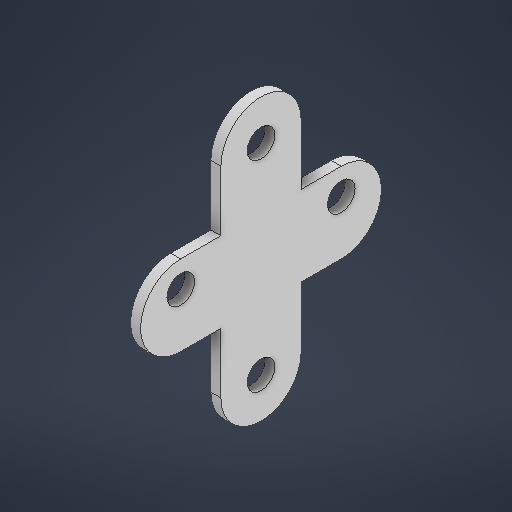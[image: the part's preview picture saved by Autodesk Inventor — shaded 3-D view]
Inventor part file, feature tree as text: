
AUTODESK INVENTOR PART (.ipt)
format: ipt  version: 2025.2 (Build 292293000, 293)  size: 212,992 bytes
history: native  units: in
note: dims shown in document units (in); Inventor stores cm internally (conversion verified against a paired STEP export)
features: extrude x1, sketch x1
ambient origin geometry x8: Origin, YZ Plane, XZ Plane, XY Plane, X Axis, Y Axis, Z Axis, Center Point
bodies: Solid1 (feature_tree)
feature tree (2):
  extrude  "Extrusion1"  Depth=0.25in
  sketch  "Sketch1"  dims[d16=0.0625in d17=0.0in d18=0.25in d20=0.172in d21=0.172in]
